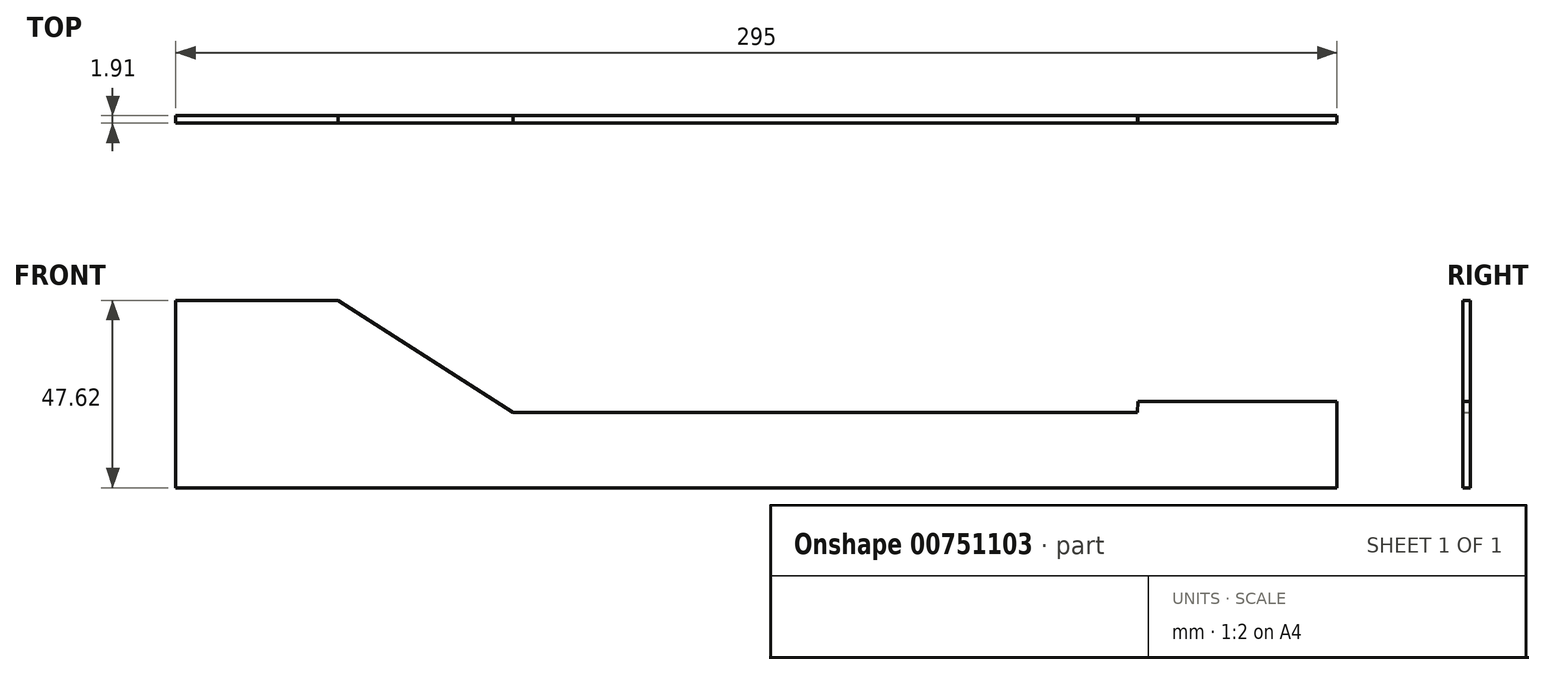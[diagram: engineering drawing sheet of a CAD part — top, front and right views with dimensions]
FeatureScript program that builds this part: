
annotation { "Feature Type Name" : "Feature", "Feature Type Description" : "" }
export const myFeature = defineFeature(function(context is Context, id is Id, definition is map)
    precondition{}
    {
        {
            var Q0;
            Q0=qCreatedBy(makeId("Front.planeOp"),FACE);
            var sketch = newSketch(context, id + "F0", { "sketchPlane" : qUnion([Q0])});
            skLineSegment(sketch, "E0", {"start": v(-134.47, 58.33) * mm, "end": v(-93.22, 58.33) * mm});
            skLineSegment(sketch, "E1", {"start": v(-93.22, 58.33) * mm, "end": v(-48.8, 29.9) * mm});
            skLineSegment(sketch, "E2", {"start": v(-48.8, 29.9) * mm, "end": v(109.83, 29.9) * mm});
            skLineSegment(sketch, "E3", {"start": v(109.83, 29.9) * mm, "end": v(110, 32.7) * mm});
            skLineSegment(sketch, "E4", {"start": v(160.53, 32.7) * mm, "end": v(110, 32.7) * mm});
            skLineSegment(sketch, "E5", {"start": v(160.53, 32.7) * mm, "end": v(160.53, 10.7) * mm});
            skLineSegment(sketch, "E6", {"start": v(160.53, 10.7) * mm, "end": v(-134.47, 10.7) * mm});
            skLineSegment(sketch, "E7", {"start": v(-134.47, 10.7) * mm, "end": v(-134.47, 58.33) * mm});
            skSolve(sketch);
        }
        {
            var Q0;
            Q0=makeQuery(id+"F0.imprint","IMPRINT",FACE,{"disambiguationData":[TD([[makeQuery(id+"F0.imprint","IMPRINT",EDGE,{"derivedFrom":sQuery(id+"F0.wireOp",EDGE,"E0")}),-1.0]])]});
            extrude(context, id + "F1", {"entities" : qUnion([Q0]), "depth" : 1.9 * mm, "offsetDistance" : 25.4 * mm});
        }
    });
